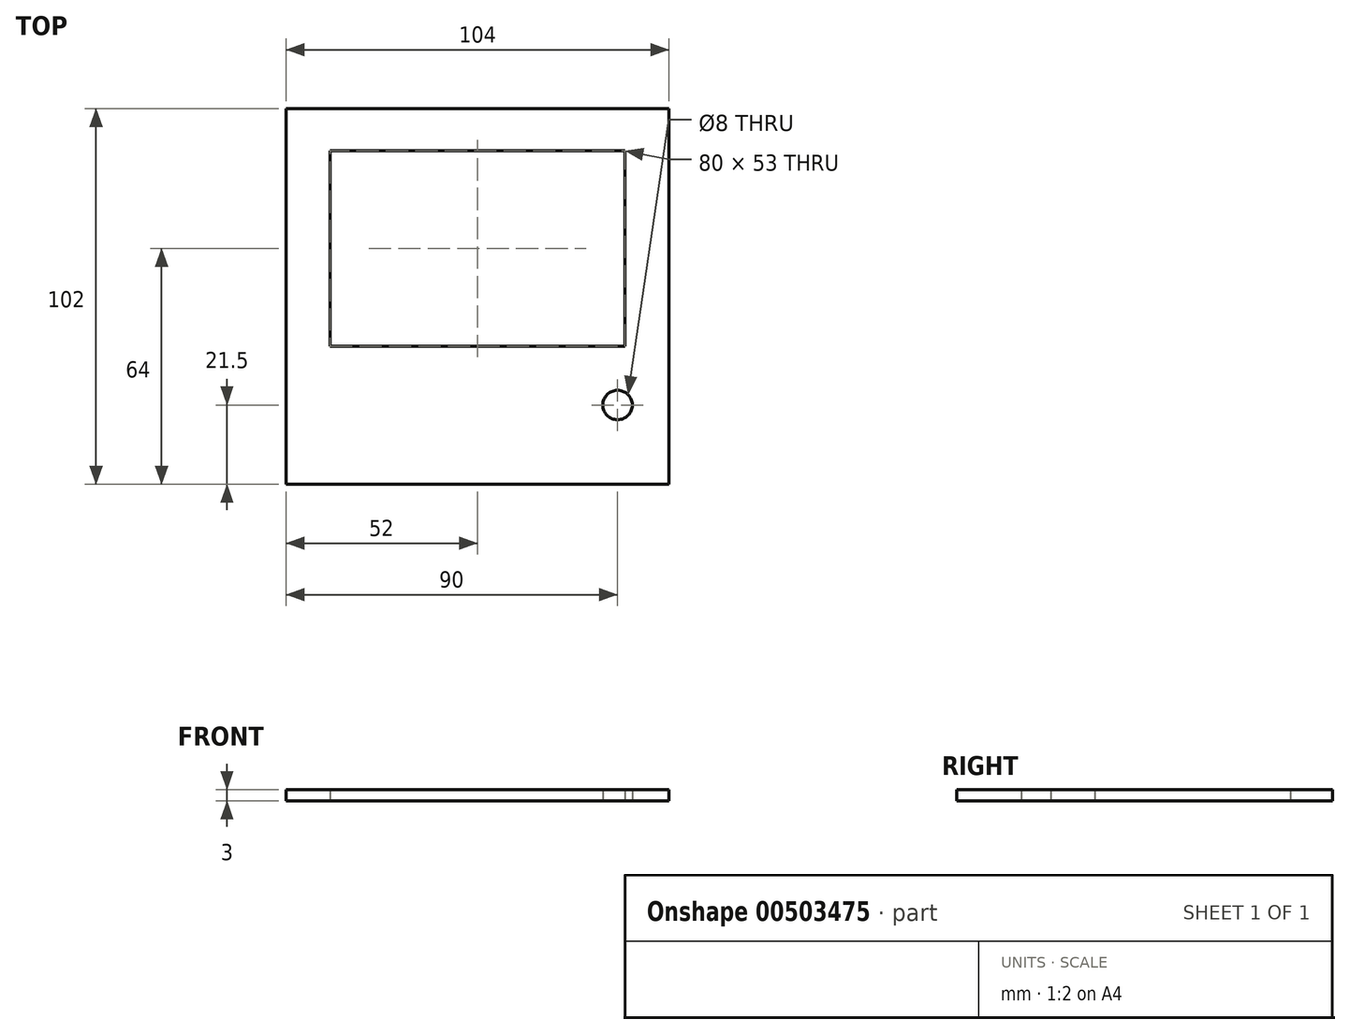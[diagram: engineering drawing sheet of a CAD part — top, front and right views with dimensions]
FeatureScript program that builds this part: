
annotation { "Feature Type Name" : "Feature", "Feature Type Description" : "" }
export const myFeature = defineFeature(function(context is Context, id is Id, definition is map)
    precondition{}
    {
        {
            var Q0;
            Q0=qCreatedBy(makeId("Top.planeOp"),FACE);
            var sketch = newSketch(context, id + "F0", { "sketchPlane" : qUnion([Q0])});
            skLineSegment(sketch, "E0.left", {"start": v(40, -26.5) * mm, "end": v(40, 26.5) * mm});
            skPoint(sketch, "E0.middle", {"position": v(0, 0) * mm});
            skLineSegment(sketch, "E1", {"start": v(0, 0) * mm, "end": v(52, 0) * mm});
            skLineSegment(sketch, "E2", {"start": v(52, 0) * mm, "end": v(52, 38) * mm});
            skLineSegment(sketch, "E3", {"start": v(52, 38) * mm, "end": v(0, 38) * mm});
            skLineSegment(sketch, "E4", {"start": v(0, 38) * mm, "end": v(0, 26.5) * mm});
            skLineSegment(sketch, "E5", {"start": v(52, 0) * mm, "end": v(52, -64) * mm});
            skLineSegment(sketch, "E6", {"start": v(52, -64) * mm, "end": v(0, -64) * mm});
            skLineSegment(sketch, "E7", {"start": v(0, -64) * mm, "end": v(0, -26.5) * mm});
            skLineSegment(sketch, "E8", {"start": v(40, 26.5) * mm, "end": v(0, 26.5) * mm});
            skLineSegment(sketch, "E9", {"start": v(40, -26.5) * mm, "end": v(0, -26.5) * mm});
            skSolve(sketch);
        }
        {
            var Q0;
            Q0 = qSketchRegion(id + "F0", true);
            extrude(context, id + "F1", {"entities" : qUnion([Q0]), "depth" : 3 * mm, "offsetDistance" : 25 * mm});
        }
        {
            var Q0;
            Q0=makeQuery(id+"F1.opExtrude","SWEPT_BODY",BODY,{"disambiguationData":[OSD([sQuery(id+"F0.wireOp",EDGE,"E0.left"),sQuery(id+"F0.wireOp",EDGE,"E2"),sQuery(id+"F0.wireOp",EDGE,"E3"),sQuery(id+"F0.wireOp",EDGE,"E4"),sQuery(id+"F0.wireOp",EDGE,"E5"),sQuery(id+"F0.wireOp",EDGE,"E6"),sQuery(id+"F0.wireOp",EDGE,"E7"),sQuery(id+"F0.wireOp",EDGE,"E8"),sQuery(id+"F0.wireOp",EDGE,"E9")])]});
            var Q1;
            Q1=qCreatedBy(makeId("Right.planeOp"),FACE);
            mirror(context, id + "F2", {"operationType" : NewBodyOperationType.ADD, "entities" : qUnion([Q0]), "mirrorPlane" : qUnion([Q1])});
        }
        {
            var Q0;
            Q0=qCreatedBy(makeId("Top.planeOp"),FACE);
            var sketch = newSketch(context, id + "F3", { "sketchPlane" : qUnion([Q0])});
            skLineSegment(sketch, "E10", {"start": v(0, 0) * mm, "end": v(40, 0) * mm});
            skLineSegment(sketch, "E11", {"start": v(40, 0) * mm, "end": v(40, -26.5) * mm});
            skLineSegment(sketch, "E12", {"start": v(40, -26.5) * mm, "end": v(40, -42.5) * mm});
            skLineSegment(sketch, "E13", {"start": v(40, -42.5) * mm, "end": v(38, -42.5) * mm});
            skCircle(sketch, "E14", {"center": v(38, -42.5) * mm, "radius": 4 * mm});
            skSolve(sketch);
        }
        {
            var Q0;
            Q0=makeQuery(id+"F3.imprint","IMPRINT",FACE,{"disambiguationData":[TD([[makeQuery(id+"F3.imprint","IMPRINT",EDGE,{"derivedFrom":sQuery(id+"F3.wireOp",EDGE,"E14")}),1.0]])]});
            extrude(context, id + "F4", {"entities" : qUnion([Q0]), "depth" : 25 * mm, "offsetDistance" : 25 * mm});
        }
        {
            var Q0;
            Q0=makeQuery(id+"F4.opExtrude","SWEPT_BODY",BODY,{"disambiguationData":[OSD([sQuery(id+"F3.wireOp",EDGE,"E14")])]});
            var Q1;
            Q1=makeQuery(id+"F1.opExtrude","SWEPT_BODY",BODY,{"disambiguationData":[OSD([sQuery(id+"F0.wireOp",EDGE,"E0.left"),sQuery(id+"F0.wireOp",EDGE,"E2"),sQuery(id+"F0.wireOp",EDGE,"E3"),sQuery(id+"F0.wireOp",EDGE,"E4"),sQuery(id+"F0.wireOp",EDGE,"E5"),sQuery(id+"F0.wireOp",EDGE,"E6"),sQuery(id+"F0.wireOp",EDGE,"E7"),sQuery(id+"F0.wireOp",EDGE,"E8"),sQuery(id+"F0.wireOp",EDGE,"E9")])]});
            booleanBodies(context, id + "F5", {"operationType" : BooleanOperationType.SUBTRACTION, "tools" : qUnion([Q0]), "targets" : qUnion([Q1])});
        }
    });
